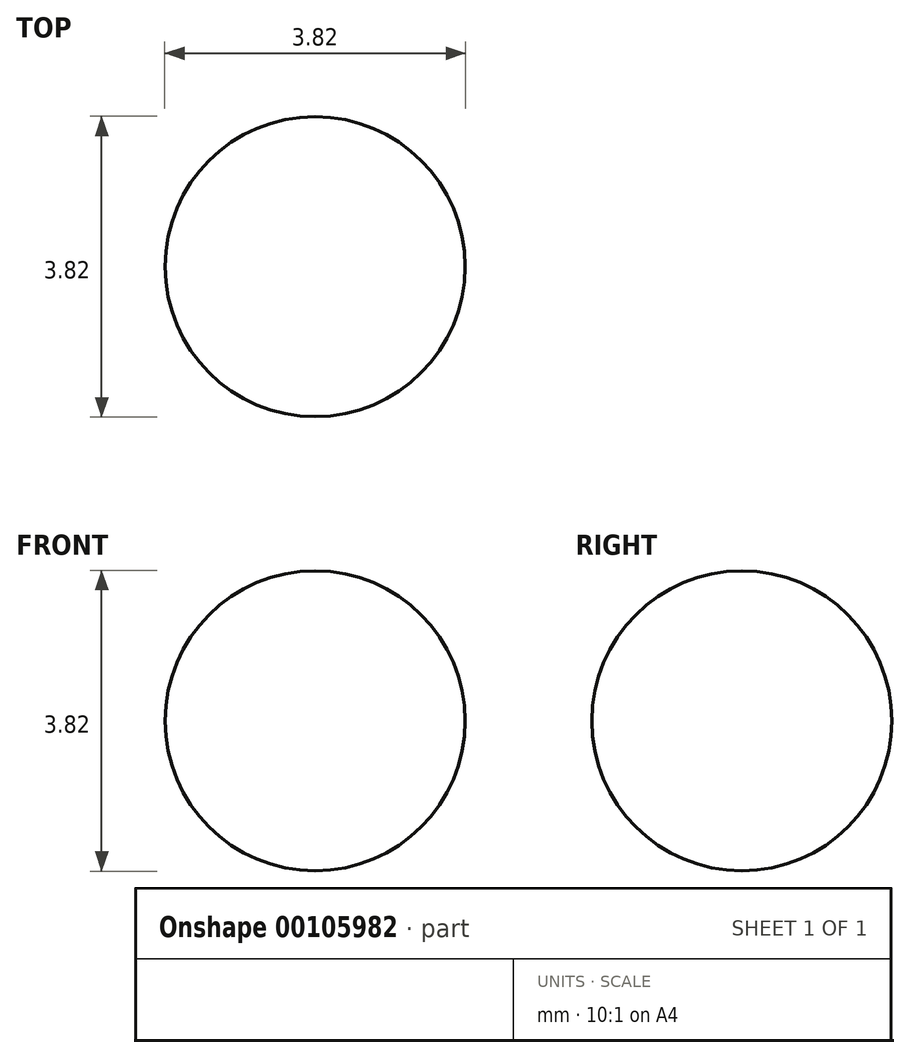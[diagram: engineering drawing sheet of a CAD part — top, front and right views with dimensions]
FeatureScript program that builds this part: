
annotation { "Feature Type Name" : "Feature", "Feature Type Description" : "" }
export const myFeature = defineFeature(function(context is Context, id is Id, definition is map)
    precondition{}
    {
        {
            var Q0;
            Q0=qCreatedBy(makeId("Front.planeOp"),FACE);
            var sketch = newSketch(context, id + "F0", { "sketchPlane" : qUnion([Q0])});
            skLineSegment(sketch, "E0.bottom", {"start": v(1.9, 1.9) * mm, "end": v(-1.9, 1.9) * mm});
            skLineSegment(sketch, "E0.top", {"start": v(1.9, -1.9) * mm, "end": v(-1.9, -1.9) * mm});
            skLineSegment(sketch, "E0.left", {"start": v(1.9, 1.9) * mm, "end": v(1.9, -1.9) * mm});
            skLineSegment(sketch, "E0.right", {"start": v(-1.9, 1.9) * mm, "end": v(-1.9, -1.9) * mm});
            skPoint(sketch, "E0.middle", {"position": v(0, 0) * mm});
            skSolve(sketch);
        }
        {
            var Q0;
            Q0=makeQuery(id+"F0.imprint","IMPRINT",FACE,{"disambiguationData":[TD([[makeQuery(id+"F0.imprint","IMPRINT",EDGE,{"derivedFrom":sQuery(id+"F0.wireOp",EDGE,"E0.bottom")}),1.0]])]});
            extrude(context, id + "F1", {"entities" : qUnion([Q0]), "depth" : 1.9 * mm, "hasSecondDirection" : true, "secondDirectionOppositeDirection" : true, "secondDirectionDepth" : 1.9 * mm});
        }
        {
            var Q0;
            Q0=makeQuery(id+"F1.opExtrude","CAP_FACE",FACE,{"disambiguationData":[OSD([sQuery(id+"F0.wireOp",EDGE,"E0.bottom"),sQuery(id+"F0.wireOp",EDGE,"E0.top"),sQuery(id+"F0.wireOp",EDGE,"E0.left"),sQuery(id+"F0.wireOp",EDGE,"E0.right")])],"isStart":false});
            var Q1;
            Q1=makeQuery(id+"F1.opExtrude","SWEPT_FACE",FACE,{"disambiguationData":[OSD([sQuery(id+"F0.wireOp",EDGE,"E0.bottom")])]});
            var Q2;
            Q2=makeQuery(id+"F1.opExtrude","SWEPT_FACE",FACE,{"disambiguationData":[OSD([sQuery(id+"F0.wireOp",EDGE,"E0.left")])]});
            var Q3;
            Q3=makeQuery(id+"F1.opExtrude","CAP_FACE",FACE,{"disambiguationData":[OSD([sQuery(id+"F0.wireOp",EDGE,"E0.bottom"),sQuery(id+"F0.wireOp",EDGE,"E0.top"),sQuery(id+"F0.wireOp",EDGE,"E0.left"),sQuery(id+"F0.wireOp",EDGE,"E0.right")])],"isStart":true});
            var Q4;
            Q4=makeQuery(id+"F1.opExtrude","SWEPT_FACE",FACE,{"disambiguationData":[OSD([sQuery(id+"F0.wireOp",EDGE,"E0.top")])]});
            var Q5;
            Q5=makeQuery(id+"F1.opExtrude","SWEPT_FACE",FACE,{"disambiguationData":[OSD([sQuery(id+"F0.wireOp",EDGE,"E0.right")])]});
            fillet(context, id + "F2", {"entities" : qUnion([Q0, Q1, Q2, Q3, Q4, Q5]), "radius" : 1.9 * mm, "tangentPropagation" : true, "allowEdgeOverflow" : false});
        }
    });
